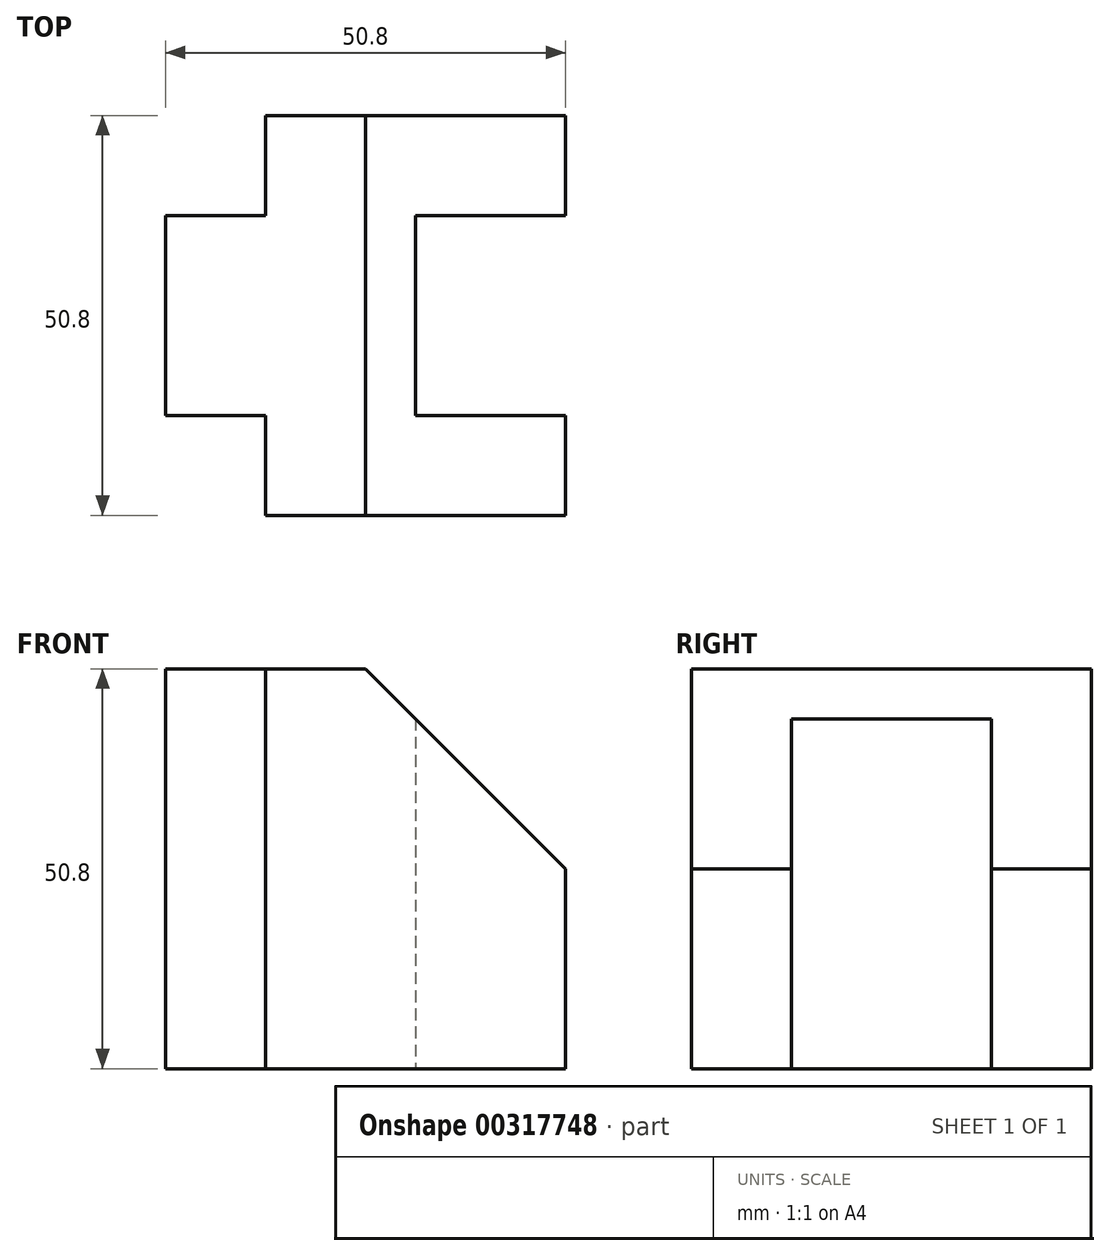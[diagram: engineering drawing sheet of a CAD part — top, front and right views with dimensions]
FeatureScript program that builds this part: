
annotation { "Feature Type Name" : "Feature", "Feature Type Description" : "" }
export const myFeature = defineFeature(function(context is Context, id is Id, definition is map)
    precondition{}
    {
        {
            var Q0;
            Q0=qCreatedBy(makeId("Front.planeOp"),FACE);
            var sketch = newSketch(context, id + "F0", { "sketchPlane" : qUnion([Q0])});
            skLineSegment(sketch, "E0", {"start": v(0, 0) * mm, "end": v(0, 50.8) * mm});
            skLineSegment(sketch, "E1", {"start": v(0, 50.8) * mm, "end": v(25.4, 50.8) * mm});
            skLineSegment(sketch, "E2", {"start": v(25.4, 50.8) * mm, "end": v(50.8, 25.4) * mm});
            skLineSegment(sketch, "E3", {"start": v(50.8, 25.4) * mm, "end": v(50.8, 0) * mm});
            skLineSegment(sketch, "E4", {"start": v(50.8, 0) * mm, "end": v(0, 0) * mm});
            skSolve(sketch);
        }
        {
            var Q0;
            Q0=makeQuery(id+"F0.imprint","IMPRINT",FACE,{"disambiguationData":[TD([[makeQuery(id+"F0.imprint","IMPRINT",EDGE,{"derivedFrom":sQuery(id+"F0.wireOp",EDGE,"E0")}),-1.0]])]});
            extrude(context, id + "F1", {"entities" : qUnion([Q0]), "depth" : 50.8 * mm});
        }
        {
            var Q0;
            Q0=makeQuery(id+"F1.opExtrude","SWEPT_FACE",FACE,{"disambiguationData":[OSD([sQuery(id+"F0.wireOp",EDGE,"E1")])]});
            var sketch = newSketch(context, id + "F2", { "sketchPlane" : qUnion([Q0])});
            skLineSegment(sketch, "E5.bottom", {"start": v(0, 0) * mm, "end": v(12.7, 0) * mm});
            skLineSegment(sketch, "E5.top", {"start": v(0, -12.7) * mm, "end": v(12.7, -12.7) * mm});
            skLineSegment(sketch, "E5.left", {"start": v(0, 0) * mm, "end": v(0, -12.7) * mm});
            skLineSegment(sketch, "E5.right", {"start": v(12.7, 0) * mm, "end": v(12.7, -12.7) * mm});
            skLineSegment(sketch, "E6.bottom", {"start": v(0, -50.8) * mm, "end": v(12.7, -50.8) * mm});
            skLineSegment(sketch, "E6.top", {"start": v(0, -38.1) * mm, "end": v(12.7, -38.1) * mm});
            skLineSegment(sketch, "E6.left", {"start": v(0, -50.8) * mm, "end": v(0, -38.1) * mm});
            skLineSegment(sketch, "E6.right", {"start": v(12.7, -50.8) * mm, "end": v(12.7, -38.1) * mm});
            skSolve(sketch);
        }
        {
            var Q0;
            Q0=makeQuery(id+"F2.imprint","IMPRINT",FACE,{"disambiguationData":[TD([[makeQuery(id+"F2.imprint","IMPRINT",EDGE,{"derivedFrom":sQuery(id+"F2.wireOp",EDGE,"E5.bottom")}),-1.0]])]});
            var Q1;
            Q1=makeQuery(id+"F2.imprint","IMPRINT",FACE,{"disambiguationData":[TD([[makeQuery(id+"F2.imprint","IMPRINT",EDGE,{"derivedFrom":sQuery(id+"F2.wireOp",EDGE,"E6.bottom")}),1.0]])]});
            extrude(context, id + "F3", {"entities" : qUnion([Q0, Q1]), "operationType" : NewBodyOperationType.REMOVE, "endBound" : BoundingType.THROUGH_ALL, "oppositeDirection" : true, "depth" : 25.4 * mm});
        }
        {
            var Q0;
            Q0=makeQuery(id+"F1.opExtrude","SWEPT_FACE",FACE,{"disambiguationData":[OSD([sQuery(id+"F0.wireOp",EDGE,"E4")])]});
            var sketch = newSketch(context, id + "F4", { "sketchPlane" : qUnion([Q0])});
            skLineSegment(sketch, "E7.bottom", {"start": v(50.8, 38.1) * mm, "end": v(31.75, 38.1) * mm});
            skLineSegment(sketch, "E7.top", {"start": v(50.8, 12.7) * mm, "end": v(31.75, 12.7) * mm});
            skLineSegment(sketch, "E7.left", {"start": v(50.8, 38.1) * mm, "end": v(50.8, 12.7) * mm});
            skLineSegment(sketch, "E7.right", {"start": v(31.75, 38.1) * mm, "end": v(31.75, 12.7) * mm});
            skSolve(sketch);
        }
        {
            var Q0;
            Q0=makeQuery(id+"F4.imprint","IMPRINT",FACE,{"disambiguationData":[TD([[makeQuery(id+"F4.imprint","IMPRINT",EDGE,{"derivedFrom":sQuery(id+"F4.wireOp",EDGE,"E7.bottom")}),1.0]])]});
            extrude(context, id + "F5", {"entities" : qUnion([Q0]), "operationType" : NewBodyOperationType.REMOVE, "endBound" : BoundingType.THROUGH_ALL, "oppositeDirection" : true, "depth" : 25.4 * mm});
        }
    });
